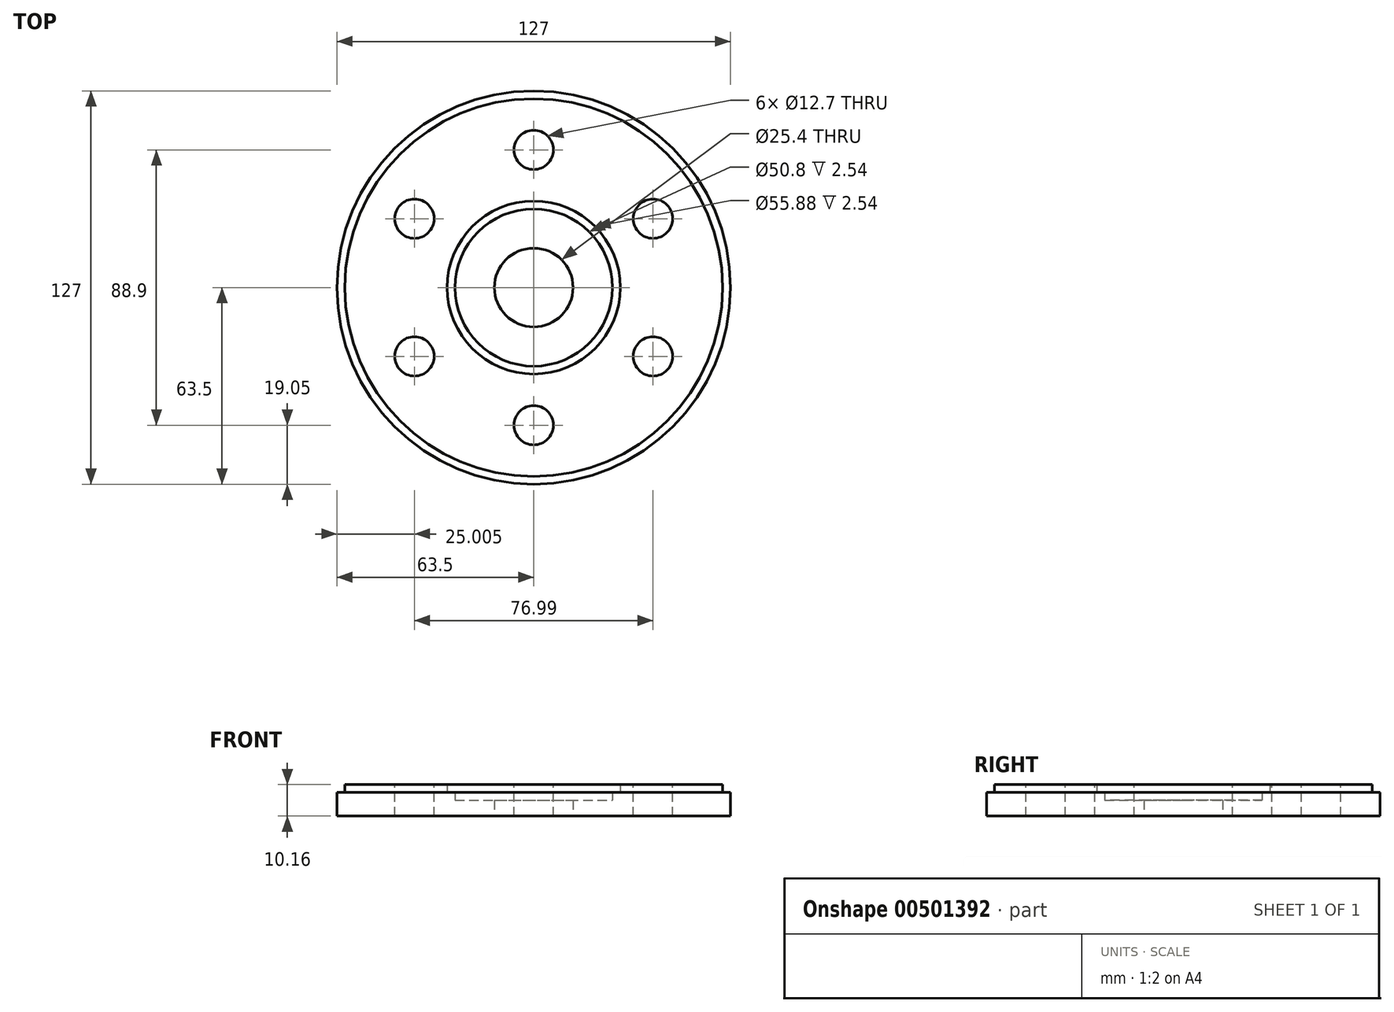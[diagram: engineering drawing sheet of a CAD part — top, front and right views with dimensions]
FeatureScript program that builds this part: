
annotation { "Feature Type Name" : "Feature", "Feature Type Description" : "" }
export const myFeature = defineFeature(function(context is Context, id is Id, definition is map)
    precondition{}
    {
        {
            var Q0;
            Q0=qCreatedBy(makeId("Right.planeOp"),FACE);
            var sketch = newSketch(context, id + "F0", { "sketchPlane" : qUnion([Q0])});
            skLineSegment(sketch, "E0", {"start": v(-12.7, 0) * mm, "end": v(-63.5, 0) * mm});
            skLineSegment(sketch, "E1", {"start": v(-63.5, 0) * mm, "end": v(-63.5, 7.62) * mm});
            skLineSegment(sketch, "E2", {"start": v(-63.5, 7.62) * mm, "end": v(-60.96, 7.62) * mm});
            skLineSegment(sketch, "E3", {"start": v(-60.96, 7.62) * mm, "end": v(-60.96, 10.16) * mm});
            skLineSegment(sketch, "E4", {"start": v(-60.96, 10.16) * mm, "end": v(-27.94, 10.16) * mm});
            skLineSegment(sketch, "E5", {"start": v(-27.94, 10.16) * mm, "end": v(-27.94, 7.62) * mm});
            skLineSegment(sketch, "E6", {"start": v(-27.94, 7.62) * mm, "end": v(-25.4, 7.62) * mm});
            skLineSegment(sketch, "E7", {"start": v(-25.4, 7.62) * mm, "end": v(-25.4, 5.08) * mm});
            skLineSegment(sketch, "E8", {"start": v(-25.4, 5.08) * mm, "end": v(-12.7, 5.08) * mm});
            skLineSegment(sketch, "E9", {"start": v(-12.7, 5.08) * mm, "end": v(-12.7, 0) * mm});
            skLineSegment(sketch, "E10", {"start": v(0, 0) * mm, "end": v(0, 42.05) * mm, "construction": true});
            skSolve(sketch);
        }
        {
            var Q0;
            Q0=makeQuery(id+"F0.imprint","IMPRINT",FACE,{"disambiguationData":[TD([[makeQuery(id+"F0.imprint","IMPRINT",EDGE,{"derivedFrom":sQuery(id+"F0.wireOp",EDGE,"E0")}),-1.0]])]});
            var Q1;
            Q1=sQuery(id+"F0.wireOp",EDGE,"E10");
            revolve(context, id + "F1", {"entities" : qUnion([Q0]), "axis" : qUnion([Q1]), "revolveType" : RevolveType.FULL});
        }
        {
            var Q0;
            Q0=makeQuery(id+"F1.opRevolve","SWEPT_FACE",FACE,{"disambiguationData":[OSD([sQuery(id+"F0.wireOp",EDGE,"E4")])]});
            var sketch = newSketch(context, id + "F2", { "sketchPlane" : qUnion([Q0])});
            skCircle(sketch, "E11", {"center": v(0, 0) * mm, "radius": 44.45 * mm, "construction": true});
            skCircle(sketch, "E12", {"center": v(0, -44.45) * mm, "radius": 6.35 * mm});
            skSolve(sketch);
        }
        {
            var Q0;
            Q0=makeQuery(id+"F2.imprint","IMPRINT",FACE,{"disambiguationData":[TD([[makeQuery(id+"F2.imprint","IMPRINT",EDGE,{"derivedFrom":sQuery(id+"F2.wireOp",EDGE,"E12")}),1.0]])]});
            extrude(context, id + "F3", {"entities" : qUnion([Q0]), "operationType" : NewBodyOperationType.REMOVE, "endBound" : BoundingType.THROUGH_ALL, "oppositeDirection" : true, "depth" : 25.4 * mm});
        }
        {
            var Q0;
            Q0=makeQuery(id+"F3.boolean.opBoolean","COPY",FACE,{"derivedFrom":makeQuery(id+"F3.opExtrude","SWEPT_FACE",FACE,{"disambiguationData":[OSD([sQuery(id+"F2.wireOp",EDGE,"E12")])]})});
            var Q1;
            Q1=sQuery(id+"F2.wireOp",EDGE,"E11");
            circularPattern(context, id + "F4", {"patternType" : PatternType.FACE, "faces" : qUnion([Q0]), "axis" : qUnion([Q1]), "angle" : 360 * degree, "instanceCount" : 6, "equalSpace" : true});
        }
    });
